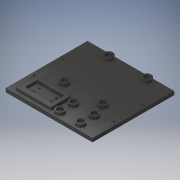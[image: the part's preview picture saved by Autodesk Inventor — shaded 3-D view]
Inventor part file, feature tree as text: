
AUTODESK INVENTOR PART (.ipt)
format: ipt  version: 2019 (Build 230136000, 136)  size: 242,176 bytes
history: native  units: in
note: dims shown in document units (in); Inventor stores cm internally (conversion verified against a paired STEP export)
features: extrude x3, sketch x3
ambient origin geometry x8: Origin, YZ Plane, XZ Plane, XY Plane, X Axis, Y Axis, Z Axis, Center Point
bodies: Solid1 (feature_tree)
feature tree (6):
  extrude  "Extrusion1"  Depth=4.5079in
  extrude  "Extrusion2"  Depth=0.1969in
  extrude  "Extrusion3"  Depth=0.1575in
  sketch  "Sketch1"  dims[d0=4.7835in d1=4.5079in]
  sketch  "Sketch3"  dims[d2=0.1969in d3=0.0in d11=0.1181in]
  sketch  "Sketch4"  dims[d12=0.9449in d13=0.1181in d14=0.1181in d15=0.1181in d16=0.9449in d17=0.9449in d20=0.9055in d21=0.9055in d22=0.315in d23=0.315in d24=0.5906in d25=0.1181in d26=0.1181in d27=0.1969in d28=0.1969in d29=1.378in d30=1.5748in d31=0.1181in d32=0.1181in d33=0.1181in d34=0.1181in d35=0.2362in d36=0.2362in d37=0.1969in d38=0.1969in d39=1.378in d40=1.5748in d41=1.2598in d42=2.126in d43=0.1181in d44=0.1181in d45=2.4409in d46=2.4409in d47=2.126in d48=1.2598in d49=0.1181in d50=0.1181in d51=0.1181in d52=0.1181in d53=0.3346in d54=0.3346in d55=0.9843in d56=1.1417in d57=0.748in d58=0.748in d59=0.9843in d60=1.1417in d61=0.1969in d62=0.0in d63=1.9291in d64=1.1024in d71=0.1969in d72=0.1575in d73=0.2362in d74=0.2756in d75=2.3228in d76=1.2598in d77=0.315in d78=0.4724in d79=0.315in d80=0.4724in d81=0.315in d82=0.4724in d83=0.315in d84=0.4724in d85=0.315in d86=0.4724in d87=0.315in d88=0.4724in d89=0.315in d90=0.4724in d91=0.315in d92=0.4724in d93=0.1575in d94=0.0in]
